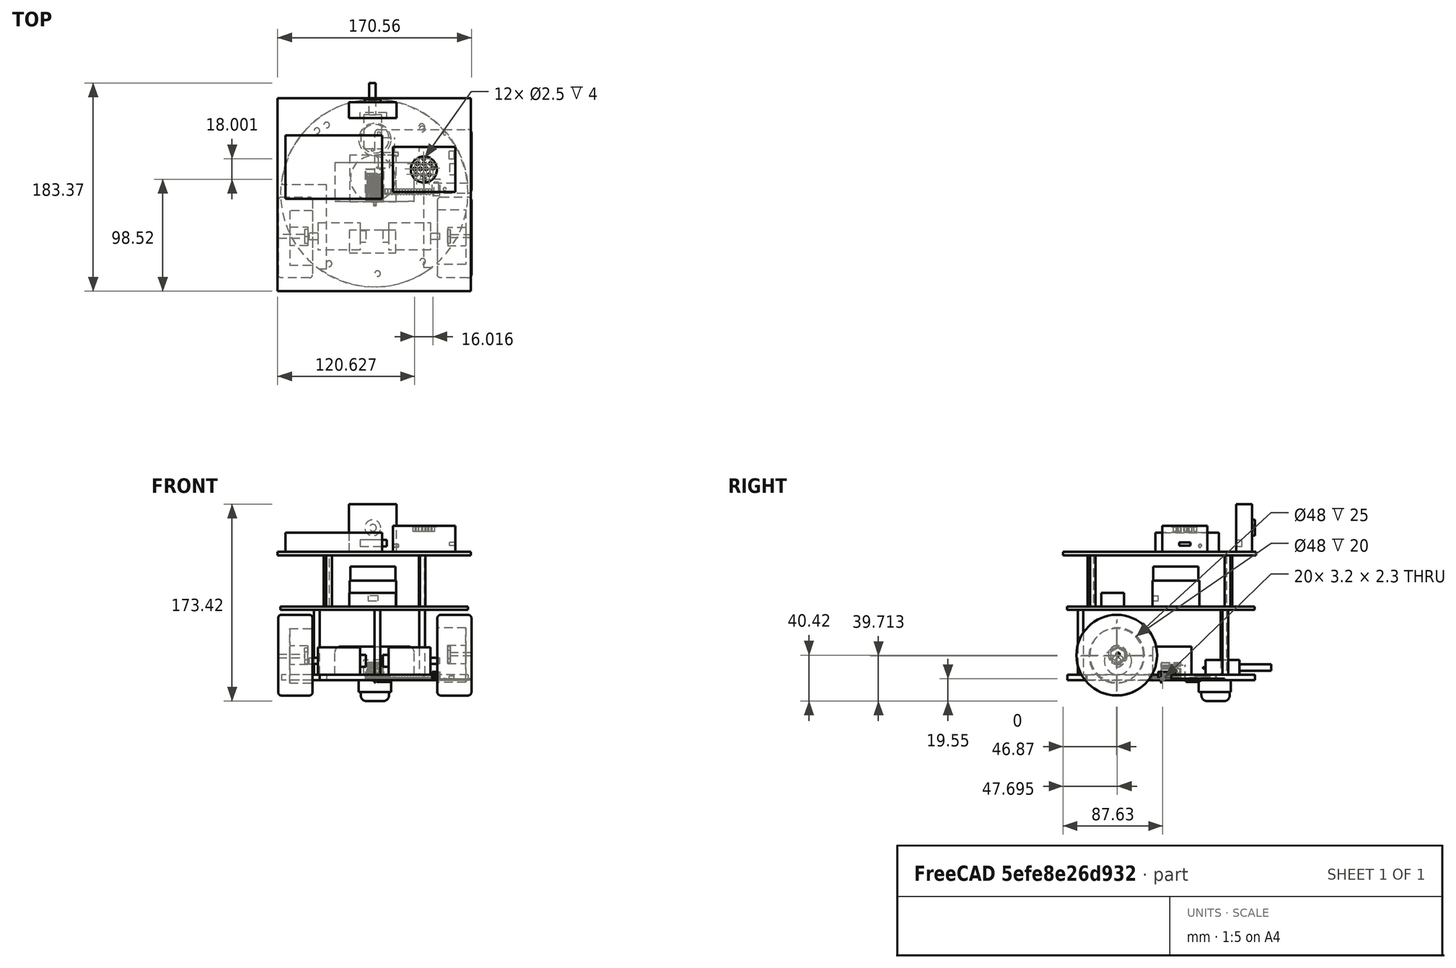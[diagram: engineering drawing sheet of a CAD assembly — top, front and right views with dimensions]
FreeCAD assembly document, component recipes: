
FREECAD ASSEMBLY — COMPONENT RECIPES ("Futbot2.0")

This assembly document has 10 components, labeled P0..P9 below (a component is one placed body or linked part). 9 of them carry a construction recipe — the FreeCAD feature program that regenerates the part from scratch, quoted from this document or its linked companion documents; the rest are supplied as boundary geometry only. No exploded tour is included for this assembly.
COMPONENT P0 — recipe-attached ("Body", modeled in this document).
Construction recipe (the document's own serialized feature program — sketch geometry with constraints, then the solid features built on it; lengths are millimeters unless a unit is written):

FEATURE [Sketcher::SketchObject] Sketch
  ArcFitTolerance = 1e-06
  AttachmentSupport = -> [XY_Plane]
  FullyConstrained = true
  MakeInternals = false
  MapMode = 5
  sketch-geometry (1):
    g0: Circle CenterX=0 CenterY=0 CenterZ=0 NormalX=0 NormalY=0 NormalZ=1 AngleXU=0 Radius=82.5
  constraints (2):
    c: Coincident(g0,g-1)
    c: Diameter(g0) = 165
FEATURE [PartDesign::Pad] Pad
  Direction = (0,0,1)
  Length = 5
  Length2 = 10
  Profile = -> Sketch
  ReferenceAxis = -> Sketch [N_Axis]
  Refine = true
  Suppressed = false
  Type = 0
FEATURE [Sketcher::SketchObject] Sketch001
  ArcFitTolerance = 1e-06
  AttachmentSupport = -> [Pad]
  FullyConstrained = false
  MakeInternals = false
  MapMode = 5
  Placement = pos=(0,0,5) rot=(0,0,1;0rad)
  sketch-geometry (8):
    g0: LineSegment StartX=-82.5394 StartY=7.37354 StartZ=0 EndX=-82.5394 EndY=-66.6265 EndZ=0
    g1: LineSegment StartX=-82.5394 StartY=-66.6265 StartZ=0 EndX=-42.5394 EndY=-66.6265 EndZ=0
    g2: LineSegment StartX=-42.5394 StartY=-66.6265 StartZ=0 EndX=-42.5394 EndY=7.37354 EndZ=0
    g3: LineSegment StartX=-42.5394 StartY=7.37354 StartZ=0 EndX=-82.5394 EndY=7.37354 EndZ=0
    g4: LineSegment StartX=42.7739 StartY=8.76566 StartZ=0 EndX=42.7739 EndY=-65.2343 EndZ=0
    g5: LineSegment StartX=42.7739 StartY=-65.2343 StartZ=0 EndX=82.7739 EndY=-65.2343 EndZ=0
    g6: LineSegment StartX=82.7739 StartY=-65.2343 StartZ=0 EndX=82.7739 EndY=8.76566 EndZ=0
    g7: LineSegment StartX=82.7739 StartY=8.76566 StartZ=0 EndX=42.7739 EndY=8.76566 EndZ=0
  constraints (20):
    c: Coincident(g0,g1)
    c: Coincident(g1,g2)
    c: Coincident(g2,g3)
    c: Coincident(g3,g0)
    c: Vertical(g0)
    c: Vertical(g2)
    c: Horizontal(g1)
    c: Horizontal(g3)
    c: Coincident(g4,g5)
    c: Coincident(g5,g6)
    c: Coincident(g6,g7)
    c: Coincident(g7,g4)
    c: Vertical(g4)
    c: Vertical(g6)
    c: Horizontal(g5)
    c: Horizontal(g7)
    c: DistanceY(g0,g0) = 74
    c: DistanceX(g3,g3) = 40
    c: DistanceX(g7,g7) = 40
    c: DistanceY(g6,g6) = 74
FEATURE [PartDesign::Pocket] Pocket
  BaseFeature = -> Pad
  Direction = (0,0,-1)
  Length = 5
  Length2 = 5
  Profile = -> Sketch001
  ReferenceAxis = -> Sketch001 [N_Axis]
  Refine = true
  Suppressed = false
  Type = 0
FEATURE [Sketcher::SketchObject] Sketch018
  ArcFitTolerance = 1e-06
  AttachmentSupport = -> [Pocket]
  FullyConstrained = false
  MakeInternals = false
  MapMode = 5
  Placement = pos=(0,0,5) rot=(0,0,1;0rad)
  sketch-geometry (4):
    g0: LineSegment StartX=-35.3299 StartY=26.6573 StartZ=0 EndX=-35.3299 EndY=-7.34269 EndZ=0
    g1: LineSegment StartX=-35.3299 StartY=-7.34269 StartZ=0 EndX=34.6701 EndY=-7.34269 EndZ=0
    g2: LineSegment StartX=34.6701 StartY=-7.34269 StartZ=0 EndX=34.6701 EndY=26.6573 EndZ=0
    g3: LineSegment StartX=34.6701 StartY=26.6573 StartZ=0 EndX=-35.3299 EndY=26.6573 EndZ=0
  constraints (10):
    c: Coincident(g0,g1)
    c: Coincident(g1,g2)
    c: Coincident(g2,g3)
    c: Coincident(g3,g0)
    c: Vertical(g0)
    c: Vertical(g2)
    c: Horizontal(g1)
    c: Horizontal(g3)
    c: DistanceY(g2,g2) = 34
    c: DistanceX(g3,g3) = 70
FEATURE [PartDesign::Pad] Pad011
  BaseFeature = -> Pocket
  Direction = (0,0,1)
  Length = 24.5
  Length2 = 10
  Profile = -> Sketch018
  ReferenceAxis = -> Sketch018 [N_Axis]
  Refine = true
  Suppressed = false
  Type = 0
FEATURE [PartDesign::Fillet] Fillet004
  Base = -> Pad011 [Vertex24,Edge35,Vertex23]
  BaseFeature = -> Pad011
  Radius = 5
  Refine = true
  SupportTransform = false
  Suppressed = false
  UseAllEdges = false
FEATURE [PartDesign::Fillet] Fillet005
  Base = -> Fillet004 [Edge21,Vertex18,Vertex5]
  BaseFeature = -> Fillet004
  Radius = 5
  Refine = true
  SupportTransform = false
  Suppressed = false
  UseAllEdges = false
FEATURE [Sketcher::SketchObject] Sketch023
  ArcFitTolerance = 1e-06
  AttachmentSupport = -> [Fillet005]
  FullyConstrained = false
  MakeInternals = false
  MapMode = 5
  Placement = pos=(0,0,5) rot=(0,0,1;0rad)
  sketch-geometry (3):
    g0: Circle CenterX=-51.0149 CenterY=54.9408 CenterZ=0 NormalX=0 NormalY=0 NormalZ=1 AngleXU=0 Radius=2.5
    g1: Circle CenterX=41.6382 CenterY=56.4611 CenterZ=0 NormalX=0 NormalY=0 NormalZ=1 AngleXU=0 Radius=2.5
    g2: Circle CenterX=2.35224 CenterY=-70.9299 CenterZ=0 NormalX=0 NormalY=0 NormalZ=1 AngleXU=0 Radius=2.5
  constraints (3):
    c: Diameter(g0) = 5
    c: Diameter(g1) = 5
    c: Diameter(g2) = 5
FEATURE [PartDesign::Pad] Pad015
  BaseFeature = -> Fillet005
  Direction = (0,0,1)
  Length = 57
  Length2 = 10
  Profile = -> Sketch023
  ReferenceAxis = -> Sketch023 [N_Axis]
  Refine = true
  Suppressed = false
  Type = 0
FEATURE [PartDesign::Plane] DatumPlane
  AttachmentSupport = -> [Pad015]
  Length = 204
  MapMode = 11
  Placement = pos=(2.35224,-70.9299,62) rot=(0,0,1;1.5708rad)
  ResizeMode = 0
  Width = 204
FEATURE [Sketcher::SketchObject] Sketch024
  ArcFitTolerance = 1e-06
  AttachmentSupport = -> [DatumPlane]
  FullyConstrained = false
  MakeInternals = false
  MapMode = 5
  Placement = pos=(2.35224,-70.9299,62) rot=(0,0,1;1.5708rad)
  sketch-geometry (1):
    g0: Circle CenterX=70.728 CenterY=2.87054 CenterZ=0 NormalX=0 NormalY=0 NormalZ=1 AngleXU=0 Radius=82.5
  constraints (1):
    c: Diameter(g0) = 165
FEATURE [PartDesign::Pad] Pad016
  BaseFeature = -> Pad015
  Direction = (0,0,1)
  Length = 3
  Length2 = 10
  Profile = -> Sketch024
  ReferenceAxis = -> Sketch024 [N_Axis]
  Refine = true
  Suppressed = false
  Type = 0
FEATURE [Sketcher::SketchObject] Sketch028
  ArcFitTolerance = 1e-06
  AttachmentSupport = -> [Pad016]
  FullyConstrained = false
  MakeInternals = false
  MapMode = 5
  Placement = pos=(0,0,65) rot=(0,0,1;0rad)
  sketch-geometry (4):
    g0: LineSegment StartX=-22.5555 StartY=-32.598 StartZ=0 EndX=-22.5555 EndY=-52.598 EndZ=0
    g1: LineSegment StartX=-22.5555 StartY=-52.598 StartZ=0 EndX=18.4445 EndY=-52.598 EndZ=0
    g2: LineSegment StartX=18.4445 StartY=-52.598 StartZ=0 EndX=18.4445 EndY=-32.598 EndZ=0
    g3: LineSegment StartX=18.4445 StartY=-32.598 StartZ=0 EndX=-22.5555 EndY=-32.598 EndZ=0
  constraints (10):
    c: Coincident(g0,g1)
    c: Coincident(g1,g2)
    c: Coincident(g2,g3)
    c: Coincident(g3,g0)
    c: Vertical(g0)
    c: Vertical(g2)
    c: Horizontal(g1)
    c: Horizontal(g3)
    c: DistanceX(g3,g3) = 41
    c: DistanceY(g2,g2) = 20
FEATURE [PartDesign::Pad] Pad019
  BaseFeature = -> Pad016
  Direction = (0,0,1)
  Length = 12
  Length2 = 10
  Profile = -> Sketch028
  ReferenceAxis = -> Sketch028 [N_Axis]
  Refine = true
  Suppressed = false
  Type = 0
FEATURE [Sketcher::SketchObject] Sketch029
  ArcFitTolerance = 1e-06
  AttachmentSupport = -> [Pad019]
  FullyConstrained = false
  MakeInternals = false
  MapMode = 5
  Placement = pos=(0,0,65) rot=(0,0,1;0rad)
  sketch-geometry (4):
    g0: Circle CenterX=-42.4666 CenterY=59.9296 CenterZ=0 NormalX=0 NormalY=0 NormalZ=1 AngleXU=0 Radius=2.5
    g1: Circle CenterX=41.2407 CenterY=58.5574 CenterZ=0 NormalX=0 NormalY=0 NormalZ=1 AngleXU=0 Radius=2.5
    g2: Circle CenterX=-40.3142 CenterY=-62.1953 CenterZ=0 NormalX=0 NormalY=0 NormalZ=1 AngleXU=0 Radius=2.5
    g3: Circle CenterX=42.0878 CenterY=-60.1323 CenterZ=0 NormalX=0 NormalY=0 NormalZ=1 AngleXU=0 Radius=2.5
  constraints (4):
    c: Diameter(g0) = 5
    c: Diameter(g1) = 5
    c: Diameter(g3) = 5
    c: Diameter(g2) = 5
FEATURE [PartDesign::Pad] Pad020
  BaseFeature = -> Pad019
  Direction = (0,0,1)
  Length = 45
  Length2 = 10
  Profile = -> Sketch029
  ReferenceAxis = -> Sketch029 [N_Axis]
  Refine = true
  Suppressed = false
  Type = 0
FEATURE [PartDesign::Plane] DatumPlane001
  AttachmentSupport = -> [Pad020]
  Length = 204
  MapMode = 11
  Placement = pos=(-42.4666,59.9296,110) rot=(0,0,1;1.5708rad)
  ResizeMode = 0
  Width = 204
FEATURE [Sketcher::SketchObject] Sketch050
  ArcFitTolerance = 1e-06
  AttachmentSupport = -> [DatumPlane001]
  FullyConstrained = false
  MakeInternals = false
  MapMode = 5
  Placement = pos=(-42.4666,59.9296,110) rot=(0,0,1;1.5708rad)
  sketch-geometry (4):
    g0: LineSegment StartX=-146.287 StartY=-126.904 StartZ=0 EndX=23.7134 EndY=-126.904 EndZ=0
    g1: LineSegment StartX=23.7134 StartY=-126.904 StartZ=0 EndX=23.7134 EndY=43.096 EndZ=0
    g2: LineSegment StartX=23.7134 StartY=43.096 StartZ=0 EndX=-146.287 EndY=43.096 EndZ=0
    g3: LineSegment StartX=-146.287 StartY=43.096 StartZ=0 EndX=-146.287 EndY=-126.904 EndZ=0
  constraints (10):
    c: Coincident(g0,g1)
    c: Coincident(g1,g2)
    c: Coincident(g2,g3)
    c: Coincident(g3,g0)
    c: Horizontal(g0)
    c: Horizontal(g2)
    c: Vertical(g1)
    c: Vertical(g3)
    c: DistanceY(g1,g1) = 170
    c: DistanceX(g0,g0) = 170
FEATURE [PartDesign::Pad] Pad024
  BaseFeature = -> Pad020
  Direction = (0,0,1)
  Length = 3
  Length2 = 10
  Profile = -> Sketch050
  ReferenceAxis = -> Sketch050 [N_Axis]
  Refine = true
  Suppressed = false
  Type = 0
FEATURE [Sketcher::SketchObject] Sketch056
  ArcFitTolerance = 1e-06
  AttachmentSupport = -> [Pad024]
  FullyConstrained = false
  MakeInternals = false
  MapMode = 5
  Placement = pos=(0,0,113) rot=(0,0,1;0rad)
  sketch-geometry (4):
    g0: LineSegment StartX=-78.7678 StartY=50.8287 StartZ=0 EndX=-78.7678 EndY=-5.17128 EndZ=0
    g1: LineSegment StartX=-78.7678 StartY=-5.17128 StartZ=0 EndX=6.23222 EndY=-5.17128 EndZ=0
    g2: LineSegment StartX=6.23222 StartY=-5.17128 StartZ=0 EndX=6.23222 EndY=50.8287 EndZ=0
    g3: LineSegment StartX=6.23222 StartY=50.8287 StartZ=0 EndX=-78.7678 EndY=50.8287 EndZ=0
  constraints (10):
    c: Coincident(g0,g1)
    c: Coincident(g1,g2)
    c: Coincident(g2,g3)
    c: Coincident(g3,g0)
    c: Vertical(g0)
    c: Vertical(g2)
    c: Horizontal(g1)
    c: Horizontal(g3)
    c: DistanceX(g3,g3) = 85
    c: DistanceY(g0,g0) = 56
FEATURE [PartDesign::Pad] Pad027
  BaseFeature = -> Pad024
  Direction = (0,0,1)
  Length = 17
  Length2 = 10
  Profile = -> Sketch056
  ReferenceAxis = -> Sketch056 [N_Axis]
  Refine = true
  Suppressed = false
  Type = 0
FEATURE [Sketcher::SketchObject] Sketch062
  ArcFitTolerance = 1e-06
  AttachmentSupport = -> [Pad027]
  FullyConstrained = false
  MakeInternals = false
  MapMode = 5
  Placement = pos=(0,0,0) rot=(1,0,0;3.14159rad)
  sketch-geometry (1):
    g0: Circle CenterX=0 CenterY=-47.1951 CenterZ=0 NormalX=0 NormalY=0 NormalZ=1 AngleXU=0 Radius=14.25
  constraints (2):
    c: PointOnObject(g0,g-2)
    c: Diameter(g0) = 28.5
FEATURE [PartDesign::Pad] Pad029
  BaseFeature = -> Pad027
  Direction = (0,0,-1)
  Length = 10.3
  Length2 = 10
  Profile = -> Sketch062
  ReferenceAxis = -> Sketch062 [N_Axis]
  Refine = true
  Suppressed = false
  Type = 0
FEATURE [Sketcher::SketchObject] Sketch063
  ArcFitTolerance = 1e-06
  AttachmentSupport = -> [Pad029]
  FullyConstrained = false
  MakeInternals = false
  MapMode = 5
  Placement = pos=(0,0,-10.3) rot=(1,0,0;3.14159rad)
  sketch-geometry (1):
    g0: Circle CenterX=0 CenterY=-47.922 CenterZ=0 NormalX=0 NormalY=0 NormalZ=1 AngleXU=0 Radius=12.5
  constraints (2):
    c: PointOnObject(g0,g-2)
    c: Diameter(g0) = 25
FEATURE [PartDesign::Pad] Pad030
  BaseFeature = -> Pad029
  Direction = (0,0,-1)
  Length = 8
  Length2 = 10
  Profile = -> Sketch063
  ReferenceAxis = -> Sketch063 [N_Axis]
  Refine = true
  Suppressed = false
  Type = 0
FEATURE [PartDesign::Fillet] Fillet020  label="Fillet021"
  Base = -> Pad030 [Face35]
  BaseFeature = -> Pad030
  Radius = 5
  Refine = true
  SupportTransform = false
  Suppressed = false
  UseAllEdges = false
FEATURE [PartDesign::Body] Body
  AllowCompound = false
  Group = -> [Sketch,Pad,Sketch001,Pocket,Sketch018,Pad011,Fillet004,Fillet005,Sketch023,Pad015,DatumPlane,Sketch024,Pad016,Sketch028,Pad019,Sketch029,Pad020,DatumPlane001,Sketch050,Pad024,Sketch056,Pad027,Sketch062,Pad029,Sketch063,Pad030,Fillet020]
  Origin = -> Origin
  Tip = -> Fillet020
COMPONENT P1 — recipe-attached ("Body001", modeled in this document).
Construction recipe (the document's own serialized feature program — sketch geometry with constraints, then the solid features built on it; lengths are millimeters unless a unit is written):

FEATURE [Sketcher::SketchObject] Sketch002
  ArcFitTolerance = 1e-06
  AttachmentSupport = -> [YZ_Plane001]
  FullyConstrained = true
  MakeInternals = false
  MapMode = 5
  Placement = pos=(0,0,0) rot=(0.57735,0.57735,0.57735;2.0944rad)
  sketch-geometry (1):
    g0: Circle CenterX=0 CenterY=0 CenterZ=0 NormalX=0 NormalY=0 NormalZ=1 AngleXU=0 Radius=12
  constraints (2):
    c: Coincident(g0,g-1)
    c: Diameter(g0) = 24
FEATURE [PartDesign::Pad] Pad001
  Direction = (1,0,0)
  Length = 37
  Length2 = 10
  Placement = pos=(0,0,0) rot=(1,1,1;2.0944rad)
  Profile = -> Sketch002
  ReferenceAxis = -> Sketch002 [N_Axis]
  Refine = true
  Suppressed = false
  Type = 0
FEATURE [Sketcher::SketchObject] Sketch003
  ArcFitTolerance = 1e-06
  AttachmentSupport = -> [Pad001]
  FullyConstrained = false
  MakeInternals = false
  MapMode = 5
  Placement = pos=(37,0,0) rot=(0.57735,0.57735,0.57735;2.0944rad)
  sketch-geometry (1):
    g0: Circle CenterX=-0.336656 CenterY=0 CenterZ=0 NormalX=0 NormalY=0 NormalZ=1 AngleXU=0 Radius=5.25
  constraints (2):
    c: PointOnObject(g0,g-1)
    c: Diameter(g0) = 10.5
FEATURE [PartDesign::Pad] Pad002
  BaseFeature = -> Pad001
  Direction = (1,0,0)
  Length = 5
  Length2 = 10
  Placement = pos=(0,0,0) rot=(1,1,1;2.0944rad)
  Profile = -> Sketch003
  ReferenceAxis = -> Sketch003 [N_Axis]
  Refine = true
  Suppressed = false
  Type = 0
FEATURE [Sketcher::SketchObject] Sketch004
  ArcFitTolerance = 1e-06
  AttachmentSupport = -> [Pad002]
  FullyConstrained = true
  MakeInternals = false
  MapMode = 5
  Placement = pos=(0,0,0) rot=(0.57735,0.57735,-0.57735;4.18879rad)
  sketch-geometry (1):
    g0: Circle CenterX=0 CenterY=0 CenterZ=0 NormalX=0 NormalY=0 NormalZ=1 AngleXU=0 Radius=2.75
  constraints (2):
    c: Coincident(g0,g-1)
    c: Diameter(g0) = 5.5
FEATURE [PartDesign::Pad] Pad003
  BaseFeature = -> Pad002
  Direction = (-1,0,0)
  Length = 8
  Length2 = 10
  Placement = pos=(0,0,0) rot=(1,1,1;2.0944rad)
  Profile = -> Sketch004
  ReferenceAxis = -> Sketch004 [N_Axis]
  Refine = true
  Suppressed = false
  Type = 0
FEATURE [PartDesign::Body] Body001
  AllowCompound = false
  Group = -> [Sketch002,Pad001,Sketch003,Pad002,Sketch004,Pad003]
  Origin = -> Origin001
  Placement = pos=(-50,-38,17) rot=(0,0,1;0rad)
  Tip = -> Pad003
COMPONENT P2 — recipe-attached ("Body002", modeled in this document).
Construction recipe (the document's own serialized feature program — sketch geometry with constraints, then the solid features built on it; lengths are millimeters unless a unit is written):

FEATURE [Sketcher::SketchObject] Sketch005
  ArcFitTolerance = 1e-06
  AttachmentSupport = -> [YZ_Plane002]
  FullyConstrained = true
  MakeInternals = false
  MapMode = 5
  Placement = pos=(0,0,0) rot=(0.57735,0.57735,0.57735;2.0944rad)
  sketch-geometry (1):
    g0: Circle CenterX=0 CenterY=0 CenterZ=0 NormalX=0 NormalY=0 NormalZ=1 AngleXU=0 Radius=12
  constraints (2):
    c: Coincident(g0,g-1)
    c: Diameter(g0) = 24
FEATURE [PartDesign::Pad] Pad004
  Direction = (1,0,0)
  Length = 37
  Length2 = 10
  Placement = pos=(0,0,0) rot=(1,1,1;2.0944rad)
  Profile = -> Sketch005
  ReferenceAxis = -> Sketch005 [N_Axis]
  Refine = true
  Suppressed = false
  Type = 0
FEATURE [Sketcher::SketchObject] Sketch006
  ArcFitTolerance = 1e-06
  AttachmentSupport = -> [Pad004]
  FullyConstrained = true
  MakeInternals = false
  MapMode = 5
  Placement = pos=(37,0,0) rot=(0.57735,0.57735,0.57735;2.0944rad)
  sketch-geometry (1):
    g0: Circle CenterX=0 CenterY=0 CenterZ=0 NormalX=0 NormalY=0 NormalZ=1 AngleXU=0 Radius=2.75
  constraints (2):
    c: Coincident(g0,g-1)
    c: Diameter(g0) = 5.5
FEATURE [PartDesign::Pad] Pad005
  BaseFeature = -> Pad004
  Direction = (1,0,0)
  Length = 8
  Length2 = 10
  Placement = pos=(0,0,0) rot=(1,1,1;2.0944rad)
  Profile = -> Sketch006
  ReferenceAxis = -> Sketch006 [N_Axis]
  Refine = true
  Suppressed = false
  Type = 0
FEATURE [Sketcher::SketchObject] Sketch007
  ArcFitTolerance = 1e-06
  AttachmentSupport = -> [Pad005]
  FullyConstrained = true
  MakeInternals = false
  MapMode = 5
  Placement = pos=(0,0,0) rot=(0.57735,0.57735,-0.57735;4.18879rad)
  sketch-geometry (1):
    g0: Circle CenterX=0 CenterY=0 CenterZ=0 NormalX=0 NormalY=0 NormalZ=1 AngleXU=0 Radius=5.25
  constraints (2):
    c: Coincident(g0,g-1)
    c: Diameter(g0) = 10.5
FEATURE [PartDesign::Pad] Pad006
  BaseFeature = -> Pad005
  Direction = (-1,0,0)
  Length = 5
  Length2 = 10
  Placement = pos=(0,0,0) rot=(1,1,1;2.0944rad)
  Profile = -> Sketch007
  ReferenceAxis = -> Sketch007 [N_Axis]
  Refine = true
  Suppressed = false
  Type = 0
FEATURE [PartDesign::Body] Body002
  AllowCompound = false
  Group = -> [Sketch005,Pad004,Sketch006,Pad005,Sketch007,Pad006]
  Origin = -> Origin002
  Placement = pos=(12,-38,17) rot=(0,0,1;0rad)
  Tip = -> Pad006
COMPONENT P3 — recipe-attached ("Body003", modeled in this document).
Construction recipe (the document's own serialized feature program — sketch geometry with constraints, then the solid features built on it; lengths are millimeters unless a unit is written):

FEATURE [Sketcher::SketchObject] Sketch008
  ArcFitTolerance = 1e-06
  AttachmentSupport = -> [YZ_Plane003]
  FullyConstrained = false
  MakeInternals = false
  MapMode = 5
  Placement = pos=(0,0,0) rot=(0.57735,0.57735,0.57735;2.0944rad)
  sketch-geometry (1):
    g0: Circle CenterX=-2.0864 CenterY=2.08625 CenterZ=0 NormalX=0 NormalY=0 NormalZ=1 AngleXU=0 Radius=35.5
  constraints (1):
    c: Diameter(g0) = 71
FEATURE [PartDesign::Pad] Pad007
  Direction = (1,0,0)
  Length = 30
  Length2 = 10
  Placement = pos=(0,0,0) rot=(1,1,1;2.0944rad)
  Profile = -> Sketch008
  ReferenceAxis = -> Sketch008 [N_Axis]
  Refine = true
  Suppressed = false
  Type = 0
FEATURE [Sketcher::SketchObject] Sketch009
  ArcFitTolerance = 1e-06
  AttachmentSupport = -> [Pad007]
  FullyConstrained = false
  MakeInternals = false
  MapMode = 5
  Placement = pos=(0,0,0) rot=(0.57735,0.57735,-0.57735;4.18879rad)
  sketch-geometry (1):
    g0: Circle CenterX=-1.66476 CenterY=-2.11974 CenterZ=0 NormalX=0 NormalY=0 NormalZ=1 AngleXU=0 Radius=24
  constraints (1):
    c: Diameter(g0) = 48
FEATURE [PartDesign::Pocket] Pocket001
  BaseFeature = -> Pad007
  Direction = (1,0,0)
  Length = 25
  Length2 = 5
  Placement = pos=(0,0,0) rot=(1,1,1;2.0944rad)
  Profile = -> Sketch009
  ReferenceAxis = -> Sketch009 [N_Axis]
  Refine = true
  Suppressed = false
  Type = 0
FEATURE [Sketcher::SketchObject] Sketch010
  ArcFitTolerance = 1e-06
  AttachmentSupport = -> [Pocket001]
  FullyConstrained = false
  MakeInternals = false
  MapMode = 5
  Placement = pos=(25,0,0) rot=(0.57735,0.57735,-0.57735;4.18879rad)
  sketch-geometry (1):
    g0: Circle CenterX=-1.35082 CenterY=-2.73267 CenterZ=0 NormalX=0 NormalY=0 NormalZ=1 AngleXU=0 Radius=8
  constraints (1):
    c: Diameter(g0) = 16
FEATURE [PartDesign::Pad] Pad008
  BaseFeature = -> Pocket001
  Direction = (-1,0,0)
  Length = 16
  Length2 = 10
  Placement = pos=(0,0,0) rot=(1,1,1;2.0944rad)
  Profile = -> Sketch010
  ReferenceAxis = -> Sketch010 [N_Axis]
  Refine = true
  Suppressed = false
  Type = 0
FEATURE [Sketcher::SketchObject] Sketch011
  ArcFitTolerance = 1e-06
  AttachmentSupport = -> [Pad008]
  FullyConstrained = false
  MakeInternals = false
  MapMode = 5
  Placement = pos=(9,0,0) rot=(0.57735,0.57735,-0.57735;4.18879rad)
  sketch-geometry (7):
    g0: LineSegment StartX=-1.11187 StartY=4.24801 StartZ=0 EndX=-7.22276 EndY=0.700721 EndZ=0
    g1: LineSegment StartX=-7.22276 StartY=0.700721 StartZ=0 EndX=-7.20616 EndY=-6.36511 EndZ=0
    g2: LineSegment StartX=-7.20616 StartY=-6.36511 StartZ=0 EndX=-1.07867 EndY=-9.88365 EndZ=0
    g3: LineSegment StartX=-1.07867 StartY=-9.88365 StartZ=0 EndX=5.03222 EndY=-6.33636 EndZ=0
    g4: LineSegment StartX=5.03222 StartY=-6.33636 StartZ=0 EndX=5.01562 EndY=0.729474 EndZ=0
    g5: LineSegment StartX=5.01562 StartY=0.729474 StartZ=0 EndX=-1.11187 EndY=4.24801 EndZ=0
    g6: Circle [constr] CenterX=-1.09527 CenterY=-2.81782 CenterZ=0 NormalX=0 NormalY=0 NormalZ=1 AngleXU=0 Radius=7.06585
  constraints (13):
    c: Coincident(g0,g1)
    c: Coincident(g1,g2)
    c: Coincident(g2,g3)
    c: Coincident(g3,g4)
    c: Coincident(g4,g5)
    c: Coincident(g5,g0)
    c: Equal(g0, g1-g5) x5
    c: PointOnObject(g0,g6)
    c: PointOnObject(g1,g6)
    c: PointOnObject(g2,g6)
    c: PointOnObject(g3,g6)
    c: PointOnObject(g4,g6)
    c: PointOnObject(g5,g6)
FEATURE [PartDesign::Pocket] Pocket002
  BaseFeature = -> Pad008
  Direction = (1,0,0)
  Length = 2.5
  Length2 = 5
  Placement = pos=(0,0,0) rot=(1,1,1;2.0944rad)
  Profile = -> Sketch011
  ReferenceAxis = -> Sketch011 [N_Axis]
  Refine = true
  Suppressed = false
  Type = 0
FEATURE [Sketcher::SketchObject] Sketch012
  ArcFitTolerance = 1e-06
  AttachmentSupport = -> [Pocket002]
  FullyConstrained = false
  MakeInternals = false
  MapMode = 5
  Placement = pos=(11.5,0,0) rot=(0.57735,0.57735,-0.57735;4.18879rad)
  sketch-geometry (1):
    g0: Circle CenterX=-0.927213 CenterY=-2.79304 CenterZ=0 NormalX=0 NormalY=0 NormalZ=1 AngleXU=0 Radius=1.5
  constraints (1):
    c: Diameter(g0) = 3
FEATURE [PartDesign::Pocket] Pocket003
  BaseFeature = -> Pocket002
  Direction = (1,0,0)
  Length = 25
  Length2 = 5
  Placement = pos=(0,0,0) rot=(1,1,1;2.0944rad)
  Profile = -> Sketch012
  ReferenceAxis = -> Sketch012 [N_Axis]
  Refine = true
  Suppressed = false
  Type = 0
FEATURE [PartDesign::Fillet] Fillet
  Base = -> Pocket003 [Edge2]
  BaseFeature = -> Pocket003
  Placement = pos=(0,0,0) rot=(1,1,1;2.0944rad)
  Radius = 3
  Refine = true
  SupportTransform = false
  Suppressed = false
  UseAllEdges = false
FEATURE [PartDesign::Fillet] Fillet001
  Base = -> Fillet [Edge3]
  BaseFeature = -> Fillet
  Placement = pos=(0,0,0) rot=(1,1,1;2.0944rad)
  Radius = 3
  Refine = true
  SupportTransform = false
  Suppressed = false
  UseAllEdges = false
FEATURE [PartDesign::Body] Body003
  AllowCompound = false
  Group = -> [Sketch008,Pad007,Sketch009,Pocket001,Sketch010,Pad008,Sketch011,Pocket002,Sketch012,Pocket003,Fillet,Fillet001]
  Origin = -> Origin003
  Placement = pos=(55,-37,20) rot=(0,0,1;0rad)
  Tip = -> Fillet001
COMPONENT P4 — recipe-attached ("Body004", modeled in this document).
Construction recipe (the document's own serialized feature program — sketch geometry with constraints, then the solid features built on it; lengths are millimeters unless a unit is written):

FEATURE [Sketcher::SketchObject] Sketch013
  ArcFitTolerance = 1e-06
  AttachmentSupport = -> [YZ_Plane004]
  FullyConstrained = false
  MakeInternals = false
  MapMode = 5
  Placement = pos=(0,0,0) rot=(0.57735,0.57735,0.57735;2.0944rad)
  sketch-geometry (1):
    g0: Circle CenterX=-2.08628 CenterY=2.08615 CenterZ=0 NormalX=0 NormalY=0 NormalZ=1 AngleXU=0 Radius=35.5
  constraints (1):
    c: Diameter(g0) = 71
FEATURE [PartDesign::Pad] Pad009
  Direction = (1,0,0)
  Length = 30
  Length2 = 10
  Placement = pos=(0,0,0) rot=(1,1,1;2.0944rad)
  Profile = -> Sketch013
  ReferenceAxis = -> Sketch013 [N_Axis]
  Refine = true
  Suppressed = false
  Type = 0
FEATURE [Sketcher::SketchObject] Sketch014
  ArcFitTolerance = 1e-06
  AttachmentSupport = -> [Pad009]
  FullyConstrained = false
  MakeInternals = false
  MapMode = 5
  Placement = pos=(30,0,0) rot=(0.57735,0.57735,0.57735;2.0944rad)
  sketch-geometry (1):
    g0: Circle CenterX=-2.49007 CenterY=1.41343 CenterZ=0 NormalX=0 NormalY=0 NormalZ=1 AngleXU=0 Radius=24
  constraints (1):
    c: Diameter(g0) = 48
FEATURE [PartDesign::Fillet] Fillet002
  Base = -> Pad009 [Edge3]
  BaseFeature = -> Pad009
  Placement = pos=(0,0,0) rot=(1,1,1;2.0944rad)
  Radius = 2.5
  Refine = true
  SupportTransform = false
  Suppressed = false
  UseAllEdges = false
FEATURE [PartDesign::Fillet] Fillet003
  Base = -> Fillet002 [Edge3]
  BaseFeature = -> Fillet002
  Placement = pos=(0,0,0) rot=(1,1,1;2.0944rad)
  Radius = 2.5
  Refine = true
  SupportTransform = false
  Suppressed = false
  UseAllEdges = false
FEATURE [PartDesign::Pocket] Pocket004
  BaseFeature = -> Fillet003
  Direction = (-1,0,0)
  Length = 20
  Length2 = 5
  Placement = pos=(0,0,0) rot=(1,1,1;2.0944rad)
  Profile = -> Sketch014
  ReferenceAxis = -> Sketch014 [N_Axis]
  Refine = true
  Suppressed = false
  Type = 0
FEATURE [Sketcher::SketchObject] Sketch015
  ArcFitTolerance = 1e-06
  AttachmentSupport = -> [Pocket004]
  FullyConstrained = false
  MakeInternals = false
  MapMode = 5
  Placement = pos=(10,0,0) rot=(0.57735,0.57735,0.57735;2.0944rad)
  sketch-geometry (1):
    g0: Circle CenterX=-1.10678 CenterY=1.90225 CenterZ=0 NormalX=0 NormalY=0 NormalZ=1 AngleXU=0 Radius=8.25
  constraints (1):
    c: Diameter(g0) = 16.5
FEATURE [PartDesign::Pad] Pad010
  BaseFeature = -> Pocket004
  Direction = (1,0,0)
  Length = 16
  Length2 = 10
  Placement = pos=(0,0,0) rot=(1,1,1;2.0944rad)
  Profile = -> Sketch015
  ReferenceAxis = -> Sketch015 [N_Axis]
  Refine = true
  Suppressed = false
  Type = 0
FEATURE [Sketcher::SketchObject] Sketch016
  ArcFitTolerance = 1e-06
  AttachmentSupport = -> [Pad010]
  FullyConstrained = false
  MakeInternals = false
  MapMode = 5
  Placement = pos=(26,0,0) rot=(0.57735,0.57735,0.57735;2.0944rad)
  sketch-geometry (7):
    g0: LineSegment StartX=4.85295 StartY=4.98885 StartZ=0 EndX=-1.20923 EndY=8.48885 EndZ=0
    g1: LineSegment StartX=-1.20923 StartY=8.48885 StartZ=0 EndX=-7.27141 EndY=4.98885 EndZ=0
    g2: LineSegment StartX=-7.27141 StartY=4.98885 StartZ=0 EndX=-7.27141 EndY=-2.01115 EndZ=0
    g3: LineSegment StartX=-7.27141 StartY=-2.01115 StartZ=0 EndX=-1.20923 EndY=-5.51115 EndZ=0
    g4: LineSegment StartX=-1.20923 StartY=-5.51115 StartZ=0 EndX=4.85295 EndY=-2.01115 EndZ=0
    g5: LineSegment StartX=4.85295 StartY=-2.01115 StartZ=0 EndX=4.85295 EndY=4.98885 EndZ=0
    g6: Circle [constr] CenterX=-1.20923 CenterY=1.48885 CenterZ=0 NormalX=0 NormalY=0 NormalZ=1 AngleXU=0 Radius=7
  constraints (15):
    c: Coincident(g0,g1)
    c: Coincident(g1,g2)
    c: Coincident(g2,g3)
    c: Coincident(g3,g4)
    c: Coincident(g4,g5)
    c: Coincident(g5,g0)
    c: Equal(g0, g1-g5) x5
    c: PointOnObject(g0,g6)
    c: PointOnObject(g1,g6)
    c: PointOnObject(g2,g6)
    c: PointOnObject(g3,g6)
    c: PointOnObject(g4,g6)
    c: PointOnObject(g5,g6)
    c: Distance(g0,g0) = 7
    c: DistanceY(g5,g5) = 7
FEATURE [PartDesign::Pocket] Pocket005
  BaseFeature = -> Pad010
  Direction = (-1,0,0)
  Length = 3
  Length2 = 5
  Placement = pos=(0,0,0) rot=(1,1,1;2.0944rad)
  Profile = -> Sketch016
  ReferenceAxis = -> Sketch016 [N_Axis]
  Refine = true
  Suppressed = false
  Type = 0
FEATURE [Sketcher::SketchObject] Sketch017
  ArcFitTolerance = 1e-06
  AttachmentSupport = -> [Pocket005]
  FullyConstrained = false
  MakeInternals = false
  MapMode = 5
  Placement = pos=(23,0,0) rot=(0.57735,0.57735,0.57735;2.0944rad)
  sketch-geometry (1):
    g0: Circle CenterX=-1.04009 CenterY=1.34355 CenterZ=0 NormalX=0 NormalY=0 NormalZ=1 AngleXU=0 Radius=1.5
  constraints (1):
    c: Diameter(g0) = 3
FEATURE [PartDesign::Pocket] Pocket006
  BaseFeature = -> Pocket005
  Direction = (-1,0,0)
  Length = 25
  Length2 = 5
  Placement = pos=(0,0,0) rot=(1,1,1;2.0944rad)
  Profile = -> Sketch017
  ReferenceAxis = -> Sketch017 [N_Axis]
  Refine = true
  Suppressed = false
  Type = 0
FEATURE [PartDesign::Body] Body004
  AllowCompound = false
  Group = -> [Sketch013,Pad009,Sketch014,Fillet002,Fillet003,Pocket004,Sketch015,Pad010,Sketch016,Pocket005,Sketch017,Pocket006]
  Origin = -> Origin004
  Placement = pos=(-85,-37,20) rot=(0,0,1;0rad)
  Tip = -> Pocket006
COMPONENT P5 — recipe-attached ("Body005", modeled in this document).
Construction recipe (the document's own serialized feature program — sketch geometry with constraints, then the solid features built on it; lengths are millimeters unless a unit is written):

FEATURE [Sketcher::SketchObject] Sketch019
  ArcFitTolerance = 1e-06
  AttachmentSupport = -> [XY_Plane005]
  FullyConstrained = false
  MakeInternals = false
  MapMode = 5
  sketch-geometry (4):
    g0: LineSegment StartX=-4.70785 StartY=9.00794 StartZ=0 EndX=-4.70785 EndY=-20.9921 EndZ=0
    g1: LineSegment StartX=-4.70785 StartY=-20.9921 StartZ=0 EndX=10.8922 EndY=-20.9921 EndZ=0
    g2: LineSegment StartX=10.8922 StartY=-20.9921 StartZ=0 EndX=10.8922 EndY=9.00794 EndZ=0
    g3: LineSegment StartX=10.8922 StartY=9.00794 StartZ=0 EndX=-4.70785 EndY=9.00794 EndZ=0
  constraints (10):
    c: Coincident(g0,g1)
    c: Coincident(g1,g2)
    c: Coincident(g2,g3)
    c: Coincident(g3,g0)
    c: Vertical(g0)
    c: Vertical(g2)
    c: Horizontal(g1)
    c: Horizontal(g3)
    c: DistanceX(g1,g1) = 15.6
    c: DistanceY(g2,g2) = 30
FEATURE [PartDesign::Pad] Pad012
  Direction = (0,0,1)
  Length = 13
  Length2 = 10
  Profile = -> Sketch019
  ReferenceAxis = -> Sketch019 [N_Axis]
  Refine = true
  Suppressed = false
  Type = 0
FEATURE [Sketcher::SketchObject] Sketch020
  ArcFitTolerance = 1e-06
  AttachmentSupport = -> [Pad012]
  FullyConstrained = false
  MakeInternals = false
  MapMode = 5
  Placement = pos=(0,9.00794,0) rot=(0,0.707107,0.707107;3.14159rad)
  sketch-geometry (1):
    g0: Circle CenterX=-2.70878 CenterY=6.23385 CenterZ=0 NormalX=0 NormalY=0 NormalZ=1 AngleXU=0 Radius=2.85
  constraints (1):
    c: Diameter(g0) = 5.7
FEATURE [PartDesign::Pad] Pad013
  BaseFeature = -> Pad012
  Direction = (0,1,-2e-16)
  Length = 28
  Length2 = 10
  Profile = -> Sketch020
  ReferenceAxis = -> Sketch020 [N_Axis]
  Refine = true
  Suppressed = false
  Type = 0
FEATURE [Sketcher::SketchObject] Sketch021
  ArcFitTolerance = 1e-06
  AttachmentSupport = -> [Pad013]
  FullyConstrained = false
  MakeInternals = false
  MapMode = 5
  Placement = pos=(0,-20.9921,0) rot=(1,0,0;1.5708rad)
  sketch-geometry (1):
    g0: Circle CenterX=3.02825 CenterY=5.85558 CenterZ=0 NormalX=0 NormalY=0 NormalZ=1 AngleXU=0 Radius=0.75
  constraints (1):
    c: Diameter(g0) = 1.5
FEATURE [PartDesign::Pad] Pad014
  BaseFeature = -> Pad013
  Direction = (0,-1,2e-16)
  Length = 2
  Length2 = 10
  Profile = -> Sketch021
  ReferenceAxis = -> Sketch021 [N_Axis]
  Refine = true
  Suppressed = false
  Type = 0
FEATURE [Sketcher::SketchObject] Sketch055
  ArcFitTolerance = 1e-06
  AttachmentSupport = -> [Pad024]
  FullyConstrained = false
  MakeInternals = false
  MapMode = 5
  Placement = pos=(0,0,113) rot=(0,0,1;0rad)
  sketch-geometry (4):
    g0: LineSegment StartX=-70.0816 StartY=-9.70625 StartZ=0 EndX=-70.0816 EndY=-65.7062 EndZ=0
    g1: LineSegment StartX=-70.0816 StartY=-65.7062 StartZ=0 EndX=14.9184 EndY=-65.7062 EndZ=0
    g2: LineSegment StartX=14.9184 StartY=-65.7062 StartZ=0 EndX=14.9184 EndY=-9.70625 EndZ=0
    g3: LineSegment StartX=14.9184 StartY=-9.70625 StartZ=0 EndX=-70.0816 EndY=-9.70625 EndZ=0
  constraints (10):
    c: Coincident(g0,g1)
    c: Coincident(g1,g2)
    c: Coincident(g2,g3)
    c: Coincident(g3,g0)
    c: Vertical(g0)
    c: Vertical(g2)
    c: Horizontal(g1)
    c: Horizontal(g3)
    c: DistanceX(g3,g3) = 85
    c: DistanceY(g0,g0) = 56
FEATURE [PartDesign::Pad] Pad026
  BaseFeature = -> Pad014
  Direction = (0,0,1)
  Length = 17
  Length2 = 10
  Profile = -> Sketch055
  ReferenceAxis = -> Sketch055 [N_Axis]
  Refine = true
  Suppressed = false
  Type = 0
FEATURE [PartDesign::Body] Body005
  AllowCompound = false
  Group = -> [Sketch019,Pad012,Sketch020,Pad013,Sketch021,Pad014,Sketch055,Pad026]
  Origin = -> Origin005
  Placement = pos=(-5,60,5) rot=(0,0,1;0rad)
  Tip = -> Pad026
COMPONENT P6 — recipe-attached ("Body006", modeled in this document).
Construction recipe (the document's own serialized feature program — sketch geometry with constraints, then the solid features built on it; lengths are millimeters unless a unit is written):

FEATURE [Sketcher::SketchObject] Sketch025
  ArcFitTolerance = 1e-06
  AttachmentSupport = -> [XY_Plane006]
  FullyConstrained = false
  MakeInternals = false
  MapMode = 5
  sketch-geometry (4):
    g0: LineSegment StartX=-17.3005 StartY=23.5417 StartZ=0 EndX=-17.3005 EndY=-17.4583 EndZ=0
    g1: LineSegment StartX=-17.3005 StartY=-17.4583 StartZ=0 EndX=23.6995 EndY=-17.4583 EndZ=0
    g2: LineSegment StartX=23.6995 StartY=-17.4583 StartZ=0 EndX=23.6995 EndY=23.5417 EndZ=0
    g3: LineSegment StartX=23.6995 StartY=23.5417 StartZ=0 EndX=-17.3005 EndY=23.5417 EndZ=0
  constraints (10):
    c: Coincident(g0,g1)
    c: Coincident(g1,g2)
    c: Coincident(g2,g3)
    c: Coincident(g3,g0)
    c: Vertical(g0)
    c: Vertical(g2)
    c: Horizontal(g1)
    c: Horizontal(g3)
    c: DistanceX(g1,g1) = 41
    c: DistanceY(g0,g0) = 41
FEATURE [PartDesign::Pad] Pad017
  Direction = (0,0,1)
  Length = 22.6
  Length2 = 10
  Profile = -> Sketch025
  ReferenceAxis = -> Sketch025 [N_Axis]
  Refine = true
  Suppressed = false
  Type = 0
FEATURE [Sketcher::SketchObject] Sketch026
  ArcFitTolerance = 1e-06
  AttachmentSupport = -> [Pad017]
  FullyConstrained = false
  MakeInternals = false
  MapMode = 5
  Placement = pos=(0,0,22.6) rot=(0,0,1;0rad)
  sketch-geometry (1):
    g0: Circle CenterX=3.29703 CenterY=2.8924 CenterZ=0 NormalX=0 NormalY=0 NormalZ=1 AngleXU=0 Radius=19.8
  constraints (1):
    c: Diameter(g0) = 39.6
FEATURE [PartDesign::Pad] Pad018
  BaseFeature = -> Pad017
  Direction = (0,0,1)
  Length = 12.6
  Length2 = 10
  Profile = -> Sketch026
  ReferenceAxis = -> Sketch026 [N_Axis]
  Refine = true
  Suppressed = false
  Type = 0
FEATURE [Sketcher::SketchObject] Sketch027
  ArcFitTolerance = 1e-06
  AttachmentSupport = -> [Pad018]
  FullyConstrained = false
  MakeInternals = false
  MapMode = 5
  Placement = pos=(0,-17.4583,0) rot=(1,0,0;1.5708rad)
  sketch-geometry (5):
    g0: LineSegment StartX=-1.04287 StartY=9.49271 StartZ=0 EndX=-1.04287 EndY=4.79271 EndZ=0
    g1: LineSegment StartX=-1.04287 StartY=4.79271 StartZ=0 EndX=7.95713 EndY=4.79271 EndZ=0
    g2: LineSegment StartX=7.95713 StartY=4.79271 StartZ=0 EndX=7.95713 EndY=9.49271 EndZ=0
    g3: LineSegment StartX=7.95713 StartY=9.49271 StartZ=0 EndX=-1.04287 EndY=9.49271 EndZ=0
    g4: GeomPoint [constr] X=3.45713 Y=7.14271 Z=0
  constraints (11):
    c: Coincident(g0,g1)
    c: Coincident(g1,g2)
    c: Coincident(g2,g3)
    c: Coincident(g3,g0)
    c: Vertical(g0)
    c: Vertical(g2)
    c: Horizontal(g1)
    c: Horizontal(g3)
    c: Symmetric(g2,g0,g4)
    c: DistanceX(g3,g3) = 9
    c: DistanceY(g2,g2) = 4.7
FEATURE [PartDesign::Pocket] Pocket007
  BaseFeature = -> Pad018
  Direction = (0,1,-2e-16)
  Length = 5
  Length2 = 5
  Profile = -> Sketch027
  ReferenceAxis = -> Sketch027 [N_Axis]
  Refine = true
  Suppressed = false
  Type = 0
FEATURE [PartDesign::Body] Body006
  AllowCompound = false
  Group = -> [Sketch025,Pad017,Sketch026,Pad018,Sketch027,Pocket007]
  Origin = -> Origin006
  Placement = pos=(-5,10,65) rot=(0,0,1;0rad)
  Tip = -> Pocket007
COMPONENT P7 — recipe-attached ("Body015", modeled in this document).
Construction recipe (the document's own serialized feature program — sketch geometry with constraints, then the solid features built on it; lengths are millimeters unless a unit is written):

FEATURE [Sketcher::SketchObject] Sketch046
  ArcFitTolerance = 1e-06
  AttachmentSupport = -> [XZ_Plane022]
  FullyConstrained = false
  MakeInternals = false
  MapMode = 5
  Placement = pos=(0,0,0) rot=(1,0,0;1.5708rad)
  sketch-geometry (4):
    g0: LineSegment StartX=-12.8525 StartY=11.6213 StartZ=0 EndX=-12.8525 EndY=-30.3787 EndZ=0
    g1: LineSegment StartX=-12.8525 StartY=-30.3787 StartZ=0 EndX=29.1475 EndY=-30.3787 EndZ=0
    g2: LineSegment StartX=29.1475 StartY=-30.3787 StartZ=0 EndX=29.1475 EndY=11.6213 EndZ=0
    g3: LineSegment StartX=29.1475 StartY=11.6213 StartZ=0 EndX=-12.8525 EndY=11.6213 EndZ=0
  constraints (10):
    c: Coincident(g0,g1)
    c: Coincident(g1,g2)
    c: Coincident(g2,g3)
    c: Coincident(g3,g0)
    c: Vertical(g0)
    c: Vertical(g2)
    c: Horizontal(g1)
    c: Horizontal(g3)
    c: DistanceX(g3,g3) = 42
    c: DistanceY(g0,g0) = 42
FEATURE [PartDesign::Pad] Pad022
  Direction = (0,-1,2e-16)
  Length = 14
  Length2 = 10
  Placement = pos=(0,0,0) rot=(1,0,0;1.5708rad)
  Profile = -> Sketch046
  ReferenceAxis = -> Sketch046 [N_Axis]
  Refine = true
  Suppressed = false
  Type = 0
FEATURE [Sketcher::SketchObject] Sketch047
  ArcFitTolerance = 1e-06
  AttachmentSupport = -> [Pad022]
  FullyConstrained = false
  MakeInternals = false
  MapMode = 5
  Placement = pos=(0,-2.1e-15,0) rot=(-1,0,0;1.5708rad)
  sketch-geometry (1):
    g0: Circle CenterX=8.14286 CenterY=9.21914 CenterZ=0 NormalX=0 NormalY=0 NormalZ=1 AngleXU=0 Radius=7
  constraints (1):
    c: Diameter(g0) = 14
FEATURE [PartDesign::Pad] Pad023
  BaseFeature = -> Pad022
  Direction = (0,1,2e-16)
  Length = 2.5
  Length2 = 10
  Placement = pos=(0,0,0) rot=(1,0,0;1.5708rad)
  Profile = -> Sketch047
  ReferenceAxis = -> Sketch047 [N_Axis]
  Refine = true
  Suppressed = false
  Type = 0
FEATURE [Sketcher::SketchObject] Sketch048
  ArcFitTolerance = 1e-06
  AttachmentSupport = -> [Pad023]
  FullyConstrained = false
  MakeInternals = false
  MapMode = 5
  Placement = pos=(0,2.5,0) rot=(-1,0,0;1.5708rad)
  sketch-geometry (1):
    g0: Circle CenterX=8.27745 CenterY=9.21909 CenterZ=0 NormalX=0 NormalY=0 NormalZ=1 AngleXU=0 Radius=5.62223
FEATURE [PartDesign::Hole] Hole
  BaseFeature = -> Pad023
  CustomThreadClearance = 0
  Depth = 0.5
  DepthType = 0
  Diameter = 6
  DrillForDepth = false
  DrillPoint = 1
  DrillPointAngle = 118
  HoleCutCountersinkAngle = 90
  HoleCutCustomValues = false
  HoleCutDepth = 0
  HoleCutDiameter = 6.1
  HoleCutType = 0
  ModelThread = false
  Placement = pos=(0,0,0) rot=(1,0,0;1.5708rad)
  Profile = -> Sketch048
  Refine = true
  Suppressed = false
  Tapered = false
  TaperedAngle = 90
  ThreadClass = 0
  ThreadDepth = 0.5
  ThreadDepthType = 0
  ThreadDirection = 0
  ThreadFit = 0
  ThreadSize = 0
  ThreadType = 0
  Threaded = false
  UseCustomThreadClearance = false
FEATURE [Sketcher::SketchObject] Sketch049
  ArcFitTolerance = 1e-06
  AttachmentSupport = -> [Hole]
  FullyConstrained = false
  MakeInternals = false
  MapMode = 5
  Placement = pos=(0,-14,0) rot=(1,0,0;1.5708rad)
  sketch-geometry (4):
    g0: LineSegment StartX=-3.02818 StartY=-20.0516 StartZ=0 EndX=-3.02818 EndY=-25.5516 EndZ=0
    g1: LineSegment StartX=-3.02818 StartY=-25.5516 StartZ=0 EndX=20.4718 EndY=-25.5516 EndZ=0
    g2: LineSegment StartX=20.4718 StartY=-25.5516 StartZ=0 EndX=20.4718 EndY=-20.0516 EndZ=0
    g3: LineSegment StartX=20.4718 StartY=-20.0516 StartZ=0 EndX=-3.02818 EndY=-20.0516 EndZ=0
  constraints (10):
    c: Coincident(g0,g1)
    c: Coincident(g1,g2)
    c: Coincident(g2,g3)
    c: Coincident(g3,g0)
    c: Vertical(g0)
    c: Vertical(g2)
    c: Horizontal(g1)
    c: Horizontal(g3)
    c: DistanceX(g3,g3) = 23.5
    c: DistanceY(g0,g0) = 5.5
FEATURE [PartDesign::Pocket] Pocket008
  BaseFeature = -> Hole
  Direction = (0,1,-2e-16)
  Length = 5
  Length2 = 5
  Placement = pos=(0,0,0) rot=(1,0,0;1.5708rad)
  Profile = -> Sketch049
  ReferenceAxis = -> Sketch049 [N_Axis]
  Refine = true
  Suppressed = false
  Type = 0
FEATURE [PartDesign::Body] Body007  label="Body015"
  AllowCompound = false
  Group = -> [Sketch046,Pad022,Sketch047,Pad023,Sketch048,Hole,Sketch049,Pocket008]
  Origin = -> Origin022
  Placement = pos=(-10,80,143.5) rot=(0,0,1;0rad)
  Tip = -> Pocket008
COMPONENT P8 — recipe-attached ("Body017", modeled in this document).
Construction recipe (the document's own serialized feature program — sketch geometry with constraints, then the solid features built on it; lengths are millimeters unless a unit is written):

FEATURE [Sketcher::SketchObject] Sketch057
  ArcFitTolerance = 1e-06
  AttachmentSupport = -> [XY_Plane024]
  FullyConstrained = false
  MakeInternals = false
  MapMode = 5
  sketch-geometry (4):
    g0: LineSegment StartX=-19.2559 StartY=20.5882 StartZ=0 EndX=-19.2559 EndY=-18.9118 EndZ=0
    g1: LineSegment StartX=-19.2559 StartY=-18.9118 StartZ=0 EndX=35.7441 EndY=-18.9118 EndZ=0
    g2: LineSegment StartX=35.7441 StartY=-18.9118 StartZ=0 EndX=35.7441 EndY=20.5882 EndZ=0
    g3: LineSegment StartX=35.7441 StartY=20.5882 StartZ=0 EndX=-19.2559 EndY=20.5882 EndZ=0
  constraints (10):
    c: Coincident(g0,g1)
    c: Coincident(g1,g2)
    c: Coincident(g2,g3)
    c: Coincident(g3,g0)
    c: Vertical(g0)
    c: Vertical(g2)
    c: Horizontal(g1)
    c: Horizontal(g3)
    c: DistanceX(g3,g3) = 55
    c: DistanceY(g0,g0) = 39.5
FEATURE [PartDesign::Pad] Pad028
  Direction = (0,0,1)
  Length = 23
  Length2 = 10
  Profile = -> Sketch057
  ReferenceAxis = -> Sketch057 [N_Axis]
  Refine = true
  Suppressed = false
  Type = 0
FEATURE [Sketcher::SketchObject] Sketch058
  ArcFitTolerance = 1e-06
  AttachmentSupport = -> [Pad028]
  FullyConstrained = false
  MakeInternals = false
  MapMode = 5
  Placement = pos=(35.7441,0,0) rot=(0.57735,0.57735,0.57735;2.0944rad)
  sketch-geometry (4):
    g0: LineSegment StartX=-4.14791 StartY=8.4514 StartZ=0 EndX=-4.14791 EndY=5.4514 EndZ=0
    g1: LineSegment StartX=-4.14791 StartY=5.4514 StartZ=0 EndX=5.85209 EndY=5.4514 EndZ=0
    g2: LineSegment StartX=5.85209 StartY=5.4514 StartZ=0 EndX=5.85209 EndY=8.4514 EndZ=0
    g3: LineSegment StartX=5.85209 StartY=8.4514 StartZ=0 EndX=-4.14791 EndY=8.4514 EndZ=0
  constraints (10):
    c: Coincident(g0,g1)
    c: Coincident(g1,g2)
    c: Coincident(g2,g3)
    c: Coincident(g3,g0)
    c: Vertical(g0)
    c: Vertical(g2)
    c: Horizontal(g1)
    c: Horizontal(g3)
    c: DistanceX(g3,g3) = 10
    c: DistanceY(g2,g2) = 3
FEATURE [PartDesign::Pocket] Pocket011
  BaseFeature = -> Pad028
  Direction = (-1,0,0)
  Length = 5
  Length2 = 5
  Profile = -> Sketch058
  ReferenceAxis = -> Sketch058 [N_Axis]
  Refine = true
  Suppressed = false
  Type = 0
FEATURE [Sketcher::SketchObject] Sketch059
  ArcFitTolerance = 1e-06
  AttachmentSupport = -> [Pocket011]
  FullyConstrained = false
  MakeInternals = false
  MapMode = 5
  Placement = pos=(0,0,23) rot=(0,0,1;0rad)
  sketch-geometry (1):
    g0: Circle CenterX=8.14251 CenterY=0.739769 CenterZ=0 NormalX=0 NormalY=0 NormalZ=1 AngleXU=0 Radius=11.5
  constraints (1):
    c: Diameter(g0) = 23
FEATURE [PartDesign::Pocket] Pocket012
  BaseFeature = -> Pocket011
  Direction = (0,0,-1)
  Length = 1
  Length2 = 5
  Profile = -> Sketch059
  ReferenceAxis = -> Sketch059 [N_Axis]
  Refine = true
  Suppressed = false
  Type = 0
FEATURE [Sketcher::SketchObject] Sketch060
  ArcFitTolerance = 1e-06
  AttachmentSupport = -> [Pocket012]
  FullyConstrained = false
  MakeInternals = false
  MapMode = 5
  Placement = pos=(0,0,22) rot=(0,0,1;0rad)
  sketch-geometry (12):
    g0: Circle CenterX=2.35518 CenterY=5.85421 CenterZ=0 NormalX=0 NormalY=0 NormalZ=1 AngleXU=0 Radius=1.25
    g1: Circle CenterX=8.14253 CenterY=5.89307 CenterZ=0 NormalX=0 NormalY=0 NormalZ=1 AngleXU=0 Radius=1.25
    g2: Circle CenterX=13.9923 CenterY=6.06804 CenterZ=0 NormalX=0 NormalY=0 NormalZ=1 AngleXU=0 Radius=1.25
    g3: Circle CenterX=0.067154 CenterY=1.27817 CenterZ=0 NormalX=0 NormalY=0 NormalZ=1 AngleXU=0 Radius=1.25
    g4: Circle CenterX=5.04698 CenterY=1.41275 CenterZ=0 NormalX=0 NormalY=0 NormalZ=1 AngleXU=0 Radius=1.25
    g5: Circle CenterX=10.296 CenterY=1.41275 CenterZ=0 NormalX=0 NormalY=0 NormalZ=1 AngleXU=0 Radius=1.25
    g6: Circle CenterX=1.82863 CenterY=-3.4509 CenterZ=0 NormalX=0 NormalY=0 NormalZ=1 AngleXU=0 Radius=1.25
    g7: Circle CenterX=7.60417 CenterY=-4.10542 CenterZ=0 NormalX=0 NormalY=0 NormalZ=1 AngleXU=0 Radius=1.25
    g8: Circle CenterX=12.9878 CenterY=-3.83624 CenterZ=0 NormalX=0 NormalY=0 NormalZ=1 AngleXU=0 Radius=1.25
    g9: Circle CenterX=8.54766 CenterY=-7.83994 CenterZ=0 NormalX=0 NormalY=0 NormalZ=1 AngleXU=0 Radius=1.25
    g10: Circle CenterX=8.00794 CenterY=10.1611 CenterZ=0 NormalX=0 NormalY=0 NormalZ=1 AngleXU=0 Radius=1.25
    g11: Circle CenterX=16.0833 CenterY=1.95111 CenterZ=0 NormalX=0 NormalY=0 NormalZ=1 AngleXU=0 Radius=1.25
  constraints (12):
    c: Diameter(g10) = 2.5
    c: Diameter(g2) = 2.5
    c: Diameter(g1) = 2.5
    c: Diameter(g0) = 2.5
    c: Diameter(g3) = 2.5
    c: Diameter(g4) = 2.5
    c: Diameter(g5) = 2.5
    c: Diameter(g6) = 2.5
    c: Diameter(g7) = 2.5
    c: Diameter(g8) = 2.5
    c: Diameter(g9) = 2.5
    c: Diameter(g11) = 2.5
FEATURE [PartDesign::Pocket] Pocket013
  BaseFeature = -> Pocket012
  Direction = (0,0,-1)
  Length = 4
  Length2 = 5
  Profile = -> Sketch060
  ReferenceAxis = -> Sketch060 [N_Axis]
  Refine = true
  Suppressed = false
  Type = 0
FEATURE [Sketcher::SketchObject] Sketch061
  ArcFitTolerance = 1e-06
  AttachmentSupport = -> [Pocket013]
  FullyConstrained = false
  MakeInternals = false
  MapMode = 5
  Placement = pos=(-19.2559,0,0) rot=(0.57735,-0.57735,-0.57735;2.0944rad)
  sketch-geometry (2):
    g0: Circle CenterX=-14.3257 CenterY=5.31776 CenterZ=0 NormalX=0 NormalY=0 NormalZ=1 AngleXU=0 Radius=1.5
    g1: Circle CenterX=-14.3257 CenterY=5.31776 CenterZ=0 NormalX=0 NormalY=0 NormalZ=1 AngleXU=0 Radius=1.15
  constraints (3):
    c: Diameter(g0) = 3
    c: Coincident(g1,g0)
    c: Diameter(g1) = 2.3
FEATURE [PartDesign::Pocket] Pocket014
  BaseFeature = -> Pocket013
  Direction = (1,0,0)
  Length = 5
  Length2 = 5
  Profile = -> Sketch061
  ReferenceAxis = -> Sketch061 [N_Axis]
  Refine = true
  Suppressed = false
  Type = 0
FEATURE [PartDesign::Body] Body009  label="Body017"
  AllowCompound = false
  Group = -> [Sketch057,Pad028,Sketch058,Pocket011,Sketch059,Pocket012,Sketch060,Pocket013,Sketch061,Pocket014]
  Origin = -> Origin024
  Placement = pos=(35,20,113) rot=(0,0,1;0rad)
  Tip = -> Pocket014
COMPONENT P9 — geometry summary ("PCBA: Raspberry Pi 4B"; no construction recipe available for this part):
  bounding box: 90.1 x 58.5 x 19.0 mm
  tessellated surface: 26,090 triangles
  volume: 18599 mm^3 (19% of its bounding box)
PROVENANCE & LICENSES
A FreeCAD (.FCStd) document from a public repository crawl; recipes are the document's own serialized feature recipes (and, for linked parts, companion documents' recipes).
License: mit.
